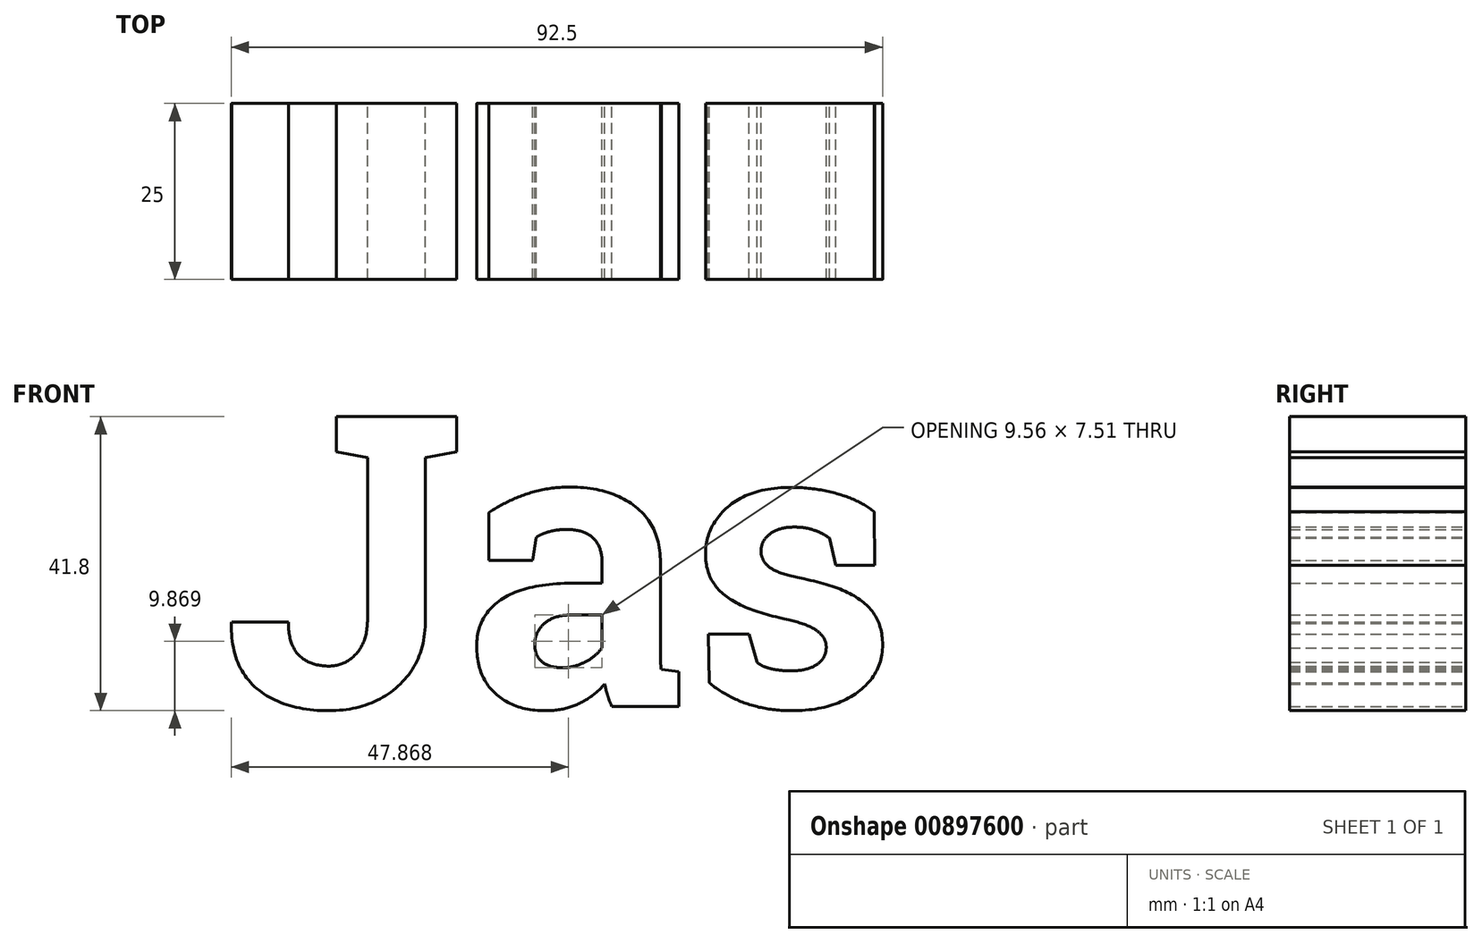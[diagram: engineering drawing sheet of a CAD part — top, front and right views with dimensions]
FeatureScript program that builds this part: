
annotation { "Feature Type Name" : "Feature", "Feature Type Description" : "" }
export const myFeature = defineFeature(function(context is Context, id is Id, definition is map)
    precondition{}
    {
        {
            var Q0;
            Q0=qCreatedBy(makeId("Front.planeOp"),FACE);
            var sketch = newSketch(context, id + "F0", { "sketchPlane" : qUnion([Q0])});
            skText(sketch, "E0", { "text": "Jas", "fontName": "RobotoSlab-Bold.ttf"});
            const initialGuessF0  = {"E0": [-0.06691, 0.00676, 1, 0, 0.04173]};
            skSetInitialGuess(sketch, initialGuessF0);
            skSolve(sketch);
        }
        {
            var Q0;
            Q0 = qSketchRegion(id + "F0", true);
            extrude(context, id + "F1", {"entities" : qUnion([Q0]), "depth" : 25 * mm, "offsetDistance" : 25.4 * mm});
        }
    });
